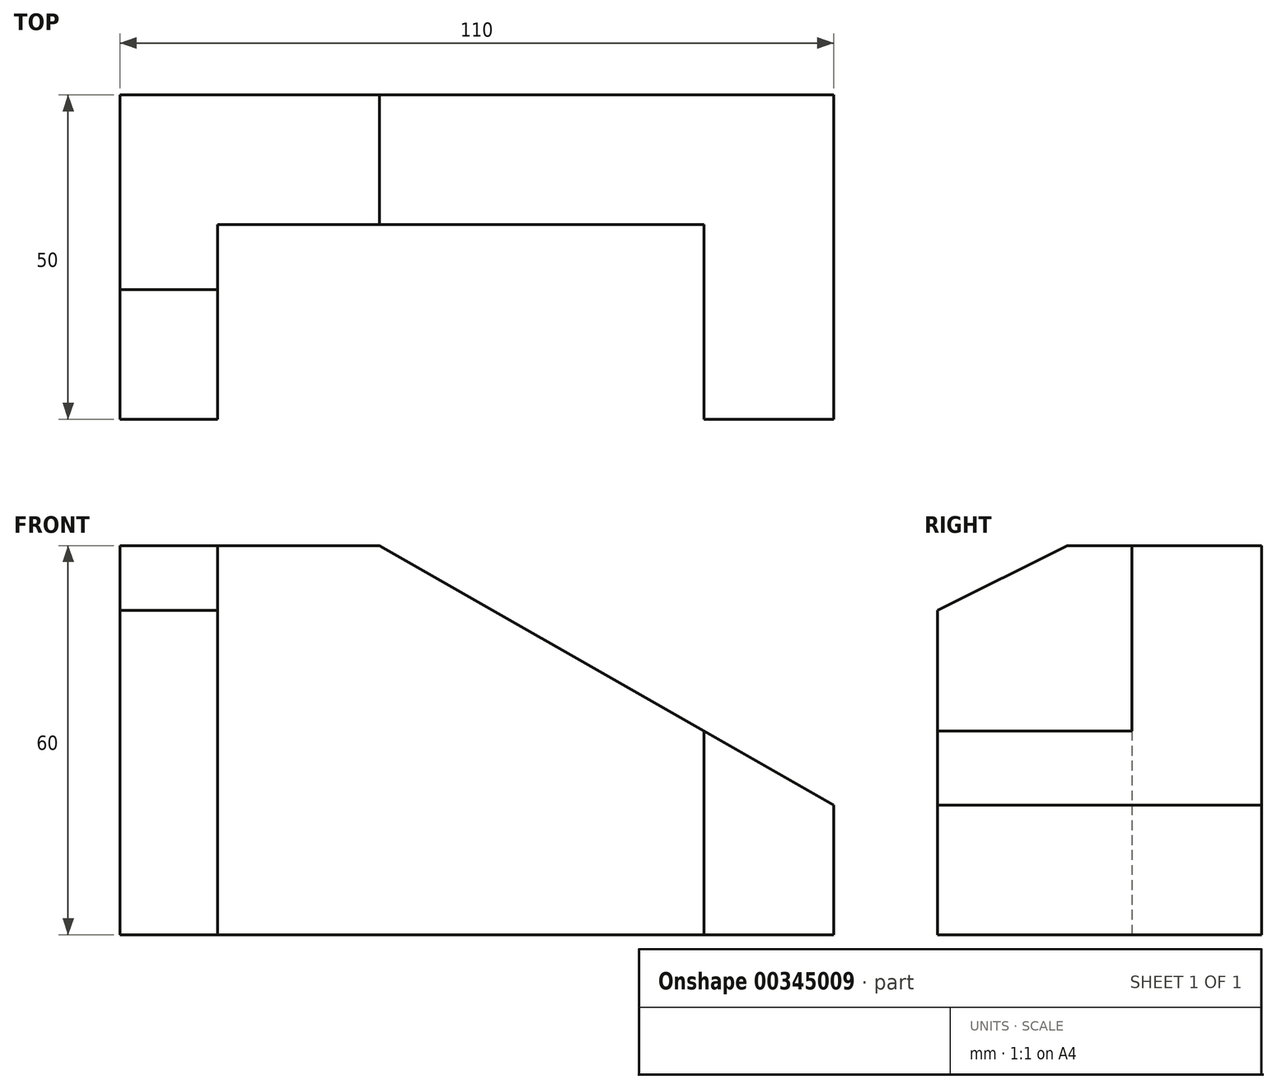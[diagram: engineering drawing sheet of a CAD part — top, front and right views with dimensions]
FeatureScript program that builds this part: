
annotation { "Feature Type Name" : "Feature", "Feature Type Description" : "" }
export const myFeature = defineFeature(function(context is Context, id is Id, definition is map)
    precondition{}
    {
        {
            var Q0;
            Q0=qCreatedBy(makeId("Top.planeOp"),FACE);
            var sketch = newSketch(context, id + "F0", { "sketchPlane" : qUnion([Q0])});
            skLineSegment(sketch, "E0", {"start": v(-51.95, 33.76) * mm, "end": v(58.05, 33.76) * mm});
            skLineSegment(sketch, "E1", {"start": v(58.05, 33.76) * mm, "end": v(58.05, -16.24) * mm});
            skLineSegment(sketch, "E2", {"start": v(58.05, -16.24) * mm, "end": v(38.05, -16.24) * mm});
            skLineSegment(sketch, "E3", {"start": v(38.05, -16.24) * mm, "end": v(38.05, 13.76) * mm});
            skLineSegment(sketch, "E4", {"start": v(38.05, 13.76) * mm, "end": v(-36.95, 13.76) * mm});
            skLineSegment(sketch, "E5", {"start": v(-36.95, 13.76) * mm, "end": v(-36.95, -16.24) * mm});
            skLineSegment(sketch, "E6", {"start": v(-36.95, -16.24) * mm, "end": v(-51.95, -16.24) * mm});
            skLineSegment(sketch, "E7", {"start": v(-51.95, -16.24) * mm, "end": v(-51.95, 33.76) * mm});
            skSolve(sketch);
        }
        {
            var Q0;
            Q0=makeQuery(id+"F0.imprint","IMPRINT",FACE,{"disambiguationData":[TD([[makeQuery(id+"F0.imprint","IMPRINT",EDGE,{"derivedFrom":sQuery(id+"F0.wireOp",EDGE,"E0")}),-1.0]])]});
            extrude(context, id + "F1", {"entities" : qUnion([Q0]), "depth" : 60 * mm});
        }
        {
            var Q0;
            Q0=makeQuery(id+"F1.opExtrude","SWEPT_FACE",FACE,{"disambiguationData":[OSD([sQuery(id+"F0.wireOp",EDGE,"E0")])]});
            var sketch = newSketch(context, id + "F2", { "sketchPlane" : qUnion([Q0])});
            skLineSegment(sketch, "E8", {"start": v(-58.05, 20) * mm, "end": v(11.95, 60) * mm});
            skLineSegment(sketch, "E9", {"start": v(11.95, 60) * mm, "end": v(-58.05, 60) * mm});
            skLineSegment(sketch, "E10", {"start": v(-58.05, 60) * mm, "end": v(-58.05, 20) * mm});
            skSolve(sketch);
        }
        {
            var Q0;
            Q0=makeQuery(id+"F2.imprint","IMPRINT",FACE,{"disambiguationData":[TD([[makeQuery(id+"F2.imprint","IMPRINT",EDGE,{"derivedFrom":sQuery(id+"F2.wireOp",EDGE,"E8")}),1.0]])]});
            extrude(context, id + "F3", {"entities" : qUnion([Q0]), "operationType" : NewBodyOperationType.REMOVE, "oppositeDirection" : true, "depth" : 50 * mm});
        }
        {
            var Q0;
            Q0=makeQuery(id+"F1.opExtrude","SWEPT_FACE",FACE,{"disambiguationData":[OSD([sQuery(id+"F0.wireOp",EDGE,"E7")])]});
            var sketch = newSketch(context, id + "F4", { "sketchPlane" : qUnion([Q0])});
            skLineSegment(sketch, "E11", {"start": v(16.24, 50) * mm, "end": v(-3.76, 60) * mm});
            skSolve(sketch);
        }
        {
            var Q0;
            {var subQ0=sQuery(id+"F4.wireOp",EDGE,"E11");Q0=makeQuery(id+"F4.imprint","IMPRINT",FACE,{"disambiguationData":[TD([[makeQuery(id+"F4.imprint","IMPRINT",EDGE,{"derivedFrom":subQ0}),-1.0]])]});}
            extrude(context, id + "F5", {"entities" : qUnion([Q0]), "operationType" : NewBodyOperationType.REMOVE, "oppositeDirection" : true, "depth" : 25 * mm});
        }
    });
